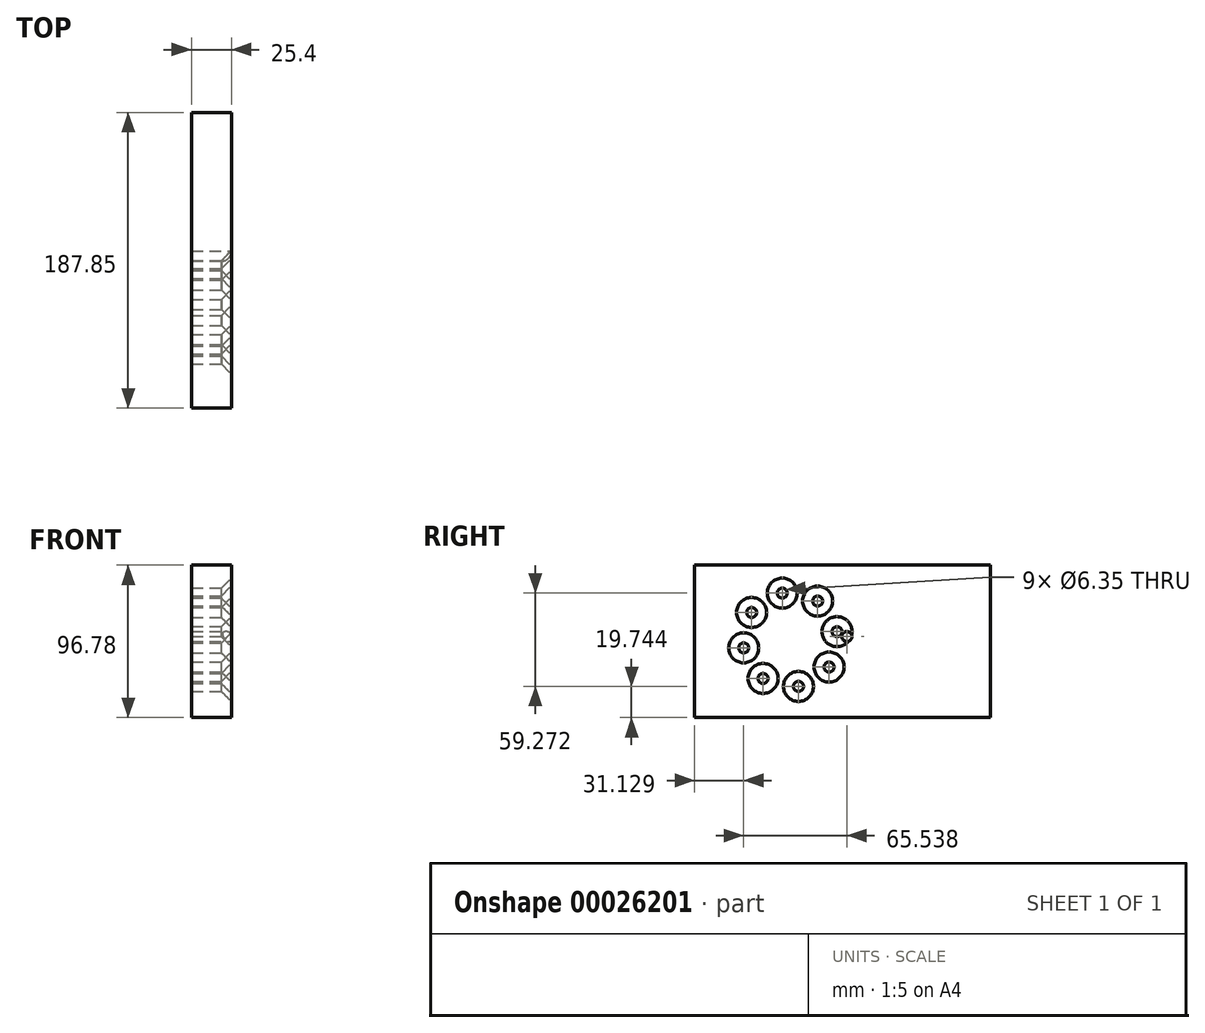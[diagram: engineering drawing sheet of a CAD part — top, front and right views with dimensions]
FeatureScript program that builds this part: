
annotation { "Feature Type Name" : "Feature", "Feature Type Description" : "" }
export const myFeature = defineFeature(function(context is Context, id is Id, definition is map)
    precondition{}
    {
        {
            var Q0;
            Q0=qCreatedBy(makeId("Right.planeOp"),FACE);
            var sketch = newSketch(context, id + "F0", { "sketchPlane" : qUnion([Q0])});
            skLineSegment(sketch, "E0.bottom", {"start": v(-45.9, 28.25) * mm, "end": v(141.95, 28.25) * mm});
            skLineSegment(sketch, "E0.top", {"start": v(-45.9, -68.53) * mm, "end": v(141.95, -68.53) * mm});
            skLineSegment(sketch, "E0.left", {"start": v(-45.9, 28.25) * mm, "end": v(-45.9, -68.53) * mm});
            skLineSegment(sketch, "E0.right", {"start": v(141.95, 28.25) * mm, "end": v(141.95, -68.53) * mm});
            skSolve(sketch);
        }
        {
            var Q0;
            Q0 = qSketchRegion(id + "F0", true);
            extrude(context, id + "F1", {"entities" : qUnion([Q0]), "depth" : 25.4 * mm});
        }
        {
            var Q0;
            Q0=makeQuery(id+"F1.opExtrude","CAP_FACE",FACE,{"disambiguationData":[OSD([sQuery(id+"F0.wireOp",EDGE,"E0.bottom"),sQuery(id+"F0.wireOp",EDGE,"E0.top"),sQuery(id+"F0.wireOp",EDGE,"E0.left"),sQuery(id+"F0.wireOp",EDGE,"E0.right")])],"isStart":false});
            var sketch = newSketch(context, id + "F2", { "sketchPlane" : qUnion([Q0])});
            skCircle(sketch, "E1", {"center": v(50.77, -17.1) * mm, "radius": 21.1 * mm});
            skSolve(sketch);
        }
        {
            var Q0;
            Q0=sQuery(id+"F2.wireOp",VERTEX,"E1.center");
            var Q1;
            Q1=makeQuery(id+"F1.opExtrude","SWEPT_BODY",BODY,{"disambiguationData":[OSD([sQuery(id+"F0.wireOp",EDGE,"E0.bottom"),sQuery(id+"F0.wireOp",EDGE,"E0.top"),sQuery(id+"F0.wireOp",EDGE,"E0.left"),sQuery(id+"F0.wireOp",EDGE,"E0.right")])]});
            hole(context, id + "F3", {"style" : HoleStyle.SIMPLE, "holeDiameter" : 6.35 * mm, "endStyle" : HoleEndStyle.THROUGH, "locations" : qUnion([Q0]), "scope" : qUnion([Q1])});
        }
        {
            var Q0;
            Q0=makeQuery(id+"F1.opExtrude","CAP_FACE",FACE,{"disambiguationData":[OSD([sQuery(id+"F0.wireOp",EDGE,"E0.bottom"),sQuery(id+"F0.wireOp",EDGE,"E0.top"),sQuery(id+"F0.wireOp",EDGE,"E0.left"),sQuery(id+"F0.wireOp",EDGE,"E0.right")])],"isStart":false});
            var sketch = newSketch(context, id + "F4", { "sketchPlane" : qUnion([Q0])});
            skLineSegment(sketch, "E2", {"start": v(-45.9, -15.73) * mm, "end": v(141.95, -15.73) * mm});
            skSolve(sketch);
        }
        {
            var Q0;
            {var subQ0=makeQuery(id+"F1.opExtrude","CAP_EDGE",EDGE,{"disambiguationData":[OSD([sQuery(id+"F0.wireOp",EDGE,"E0.bottom")])],"isStart":false});Q0=makeQuery(id+"F4.imprint","IMPRINT",FACE,{"disambiguationData":[TD([[makeQuery(id+"F4.imprint","IMPRINT",EDGE,{"derivedFrom":subQ0}),-1.0]])]});}
            var sketch = newSketch(context, id + "F5", { "sketchPlane" : qUnion([Q0])});
            skCircle(sketch, "E3.cCircle", {"center": v(14.87, -19.15) * mm, "radius": 27.79 * mm, "construction": true});
            skLineSegment(sketch, "E3.0", {"start": v(-9.73, -1.83) * mm, "end": v(9.73, 10.49) * mm});
            skLineSegment(sketch, "E3.1", {"start": v(9.73, 10.49) * mm, "end": v(32.19, 5.44) * mm});
            skLineSegment(sketch, "E3.2", {"start": v(32.19, 5.44) * mm, "end": v(44.5, -14) * mm});
            skLineSegment(sketch, "E3.3", {"start": v(44.5, -14) * mm, "end": v(39.46, -36.47) * mm});
            skLineSegment(sketch, "E3.4", {"start": v(39.46, -36.47) * mm, "end": v(20, -48.79) * mm});
            skLineSegment(sketch, "E3.5", {"start": v(20, -48.79) * mm, "end": v(-2.46, -43.74) * mm});
            skLineSegment(sketch, "E3.6", {"start": v(-2.46, -43.74) * mm, "end": v(-14.77, -24.3) * mm});
            skLineSegment(sketch, "E3.7", {"start": v(-14.77, -24.3) * mm, "end": v(-9.73, -1.83) * mm});
            skPoint(sketch, "E3.0.midPoint", {"position": v(0, 4.33) * mm});
            skSolve(sketch);
        }
        {
            var Q0;
            Q0=sQuery(id+"F5.wireOp",VERTEX,"E3.1.start");
            var Q1;
            Q1=sQuery(id+"F5.wireOp",VERTEX,"E3.7.end");
            var Q2;
            Q2=sQuery(id+"F5.wireOp",VERTEX,"E3.7.start");
            var Q3;
            Q3=sQuery(id+"F5.wireOp",VERTEX,"E3.6.start");
            var Q4;
            Q4=sQuery(id+"F5.wireOp",VERTEX,"E3.5.start");
            var Q5;
            Q5=sQuery(id+"F5.wireOp",VERTEX,"E3.3.end");
            var Q6;
            Q6=sQuery(id+"F5.wireOp",VERTEX,"E3.2.end");
            var Q7;
            Q7=sQuery(id+"F5.wireOp",VERTEX,"E3.2.start");
            var Q8;
            Q8=makeQuery(id+"F1.opExtrude","SWEPT_BODY",BODY,{"disambiguationData":[OSD([sQuery(id+"F0.wireOp",EDGE,"E0.bottom"),sQuery(id+"F0.wireOp",EDGE,"E0.top"),sQuery(id+"F0.wireOp",EDGE,"E0.left"),sQuery(id+"F0.wireOp",EDGE,"E0.right")])]});
            hole(context, id + "F6", {"style" : HoleStyle.C_SINK, "holeDiameter" : 6.35 * mm, "cSinkDiameter" : 19.05 * mm, "endStyle" : HoleEndStyle.THROUGH, "locations" : qUnion([Q0, Q1, Q2, Q3, Q4, Q5, Q6, Q7]), "scope" : qUnion([Q8]), "cSinkAngle" : 90 * degree});
        }
    });
